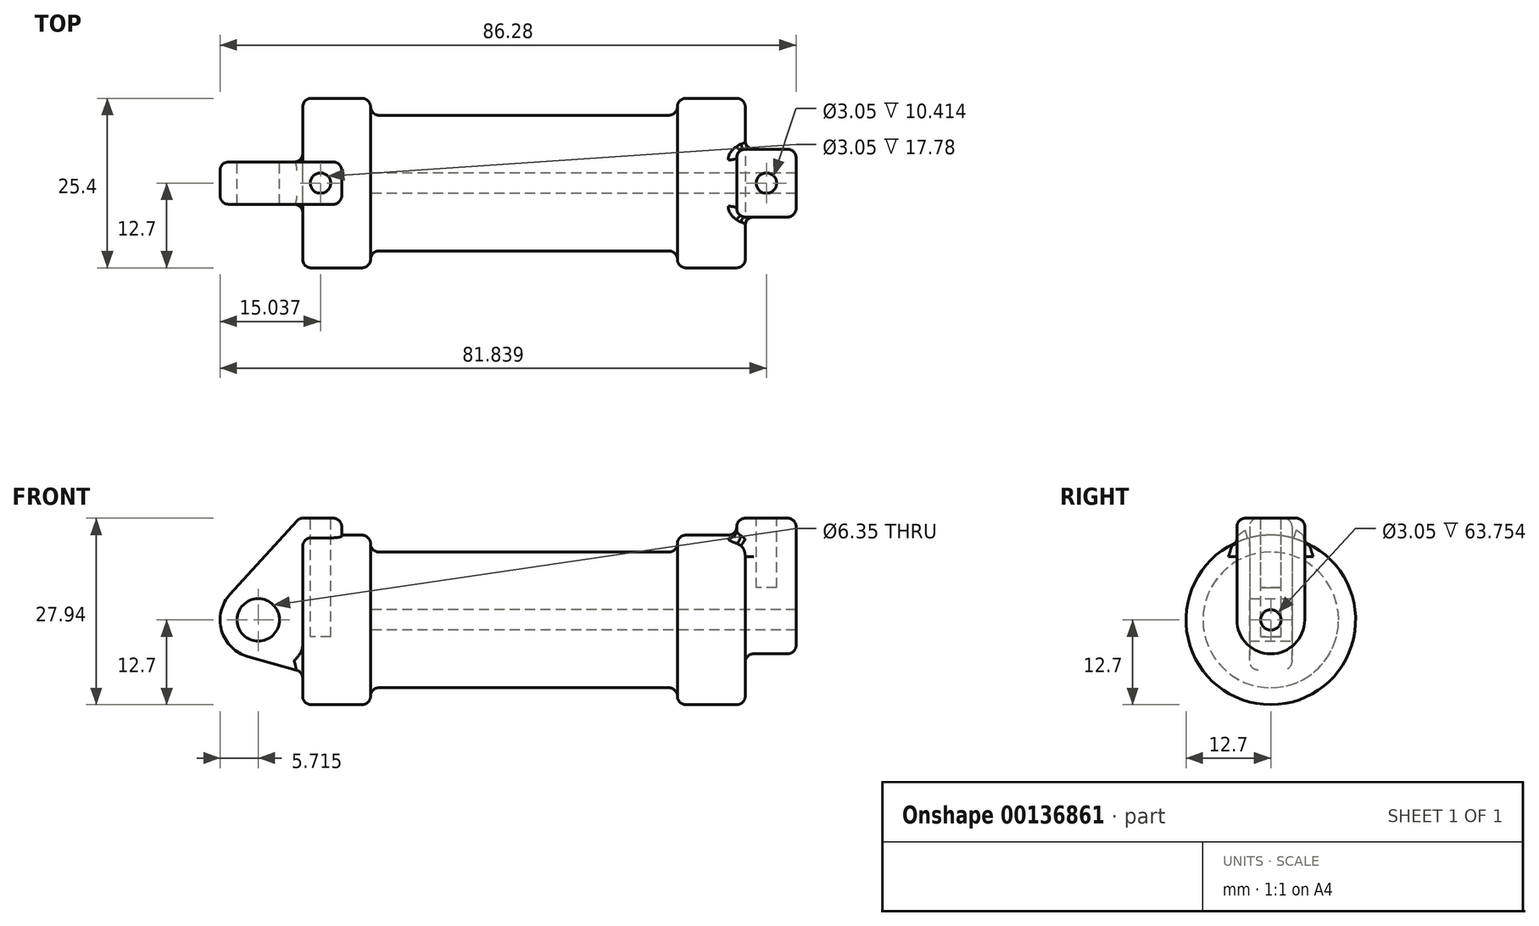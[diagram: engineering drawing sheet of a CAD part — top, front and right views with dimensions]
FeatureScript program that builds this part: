
annotation { "Feature Type Name" : "Feature", "Feature Type Description" : "" }
export const myFeature = defineFeature(function(context is Context, id is Id, definition is map)
    precondition{}
    {
        {
            var Q0;
            Q0=qCreatedBy(makeId("Front.planeOp"),FACE);
            var sketch = newSketch(context, id + "F0", { "sketchPlane" : qUnion([Q0])});
            skLineSegment(sketch, "E0", {"start": v(0, 0) * mm, "end": v(0, 12.7) * mm});
            skLineSegment(sketch, "E1", {"start": v(0, 12.7) * mm, "end": v(10.16, 12.7) * mm});
            skLineSegment(sketch, "E2", {"start": v(10.16, 12.7) * mm, "end": v(10.16, 10.16) * mm});
            skLineSegment(sketch, "E3", {"start": v(10.16, 10.16) * mm, "end": v(56.13, 10.16) * mm});
            skLineSegment(sketch, "E4", {"start": v(56.13, 10.16) * mm, "end": v(56.13, 12.7) * mm});
            skLineSegment(sketch, "E5", {"start": v(56.13, 12.7) * mm, "end": v(66.3, 12.7) * mm});
            skLineSegment(sketch, "E6", {"start": v(66.3, 12.7) * mm, "end": v(66.3, 0) * mm});
            skLineSegment(sketch, "E7", {"start": v(66.3, 0) * mm, "end": v(0, 0) * mm});
            skLineSegment(sketch, "E8", {"start": v(5.84, 15.24) * mm, "end": v(-0.5, 15.24) * mm});
            skLineSegment(sketch, "E9", {"start": v(-0.5, 15.24) * mm, "end": v(-10.88, 3.85) * mm});
            skLineSegment(sketch, "E10", {"start": v(0, 0) * mm, "end": v(-6.65, 0) * mm});
            skCircle(sketch, "E11", {"center": v(-6.65, 0) * mm, "radius": 5.72 * mm});
            skCircle(sketch, "E12", {"center": v(-6.65, 0) * mm, "radius": 3.18 * mm});
            skLineSegment(sketch, "E13", {"start": v(5.84, 15.24) * mm, "end": v(5.84, -9.4) * mm});
            skLineSegment(sketch, "E14", {"start": v(5.84, -9.4) * mm, "end": v(-8.18, -5.5) * mm});
            skSolve(sketch);
        }
        {
            var Q0;
            {var subQ0=sQuery(id+"F0.wireOp",EDGE,"E0");Q0=makeQuery(id+"F0.imprint","IMPRINT",FACE,{"disambiguationData":[TD([[makeQuery(id+"F0.imprint","IMPRINT",EDGE,{"derivedFrom":subQ0}),-1.0]])]});}
            var Q1;
            {var subQ0=sQuery(id+"F0.wireOp",EDGE,"E2");Q1=makeQuery(id+"F0.imprint","IMPRINT",FACE,{"disambiguationData":[TD([[makeQuery(id+"F0.imprint","IMPRINT",EDGE,{"derivedFrom":subQ0}),-1.0]])]});}
            var Q2;
            Q2=sQuery(id+"F0.wireOp",EDGE,"E7");
            revolve(context, id + "F1", {"entities" : qUnion([Q0, Q1]), "axis" : qUnion([Q2]), "revolveType" : RevolveType.FULL});
        }
        {
            var Q0;
            {var subQ3=sQuery(id+"F0.wireOp",EDGE,"E0");Q0=makeQuery(id+"F0.imprint","IMPRINT",FACE,{"disambiguationData":[TD([[makeQuery(id+"F0.imprint","IMPRINT",EDGE,{"derivedFrom":subQ3}),1.0]])]});}
            var Q1;
            {var subQ0=sQuery(id+"F0.wireOp",EDGE,"E0");Q1=makeQuery(id+"F0.imprint","IMPRINT",FACE,{"disambiguationData":[TD([[makeQuery(id+"F0.imprint","IMPRINT",EDGE,{"derivedFrom":subQ0}),-1.0]])]});}
            var Q2;
            {var subQ0=sQuery(id+"F0.wireOp",EDGE,"E14");Q2=makeQuery(id+"F0.imprint","IMPRINT",FACE,{"disambiguationData":[TD([[makeQuery(id+"F0.imprint","IMPRINT",EDGE,{"derivedFrom":subQ0}),-1.0]])]});}
            var Q3;
            {var subQ4=sQuery(id+"F0.wireOp",EDGE,"E12");Q3=makeQuery(id+"F0.imprint","IMPRINT",FACE,{"disambiguationData":[TD([[makeQuery(id+"F0.imprint","IMPRINT",EDGE,{"derivedFrom":subQ4}),-1.0]])]});}
            extrude(context, id + "F2", {"entities" : qUnion([Q0, Q1, Q2, Q3]), "operationType" : NewBodyOperationType.ADD, "endBound" : BoundingType.SYMMETRIC, "depth" : 6.35 * mm});
        }
        {
            var Q0;
            Q0=makeQuery(id+"F1.opRevolve","SWEPT_FACE",FACE,{"disambiguationData":[OSD([sQuery(id+"F0.wireOp",EDGE,"E6")])]});
            var sketch = newSketch(context, id + "F3", { "sketchPlane" : qUnion([Q0])});
            skCircle(sketch, "E15", {"center": v(0, 0) * mm, "radius": 1.52 * mm});
            skCircle(sketch, "E16", {"center": v(0, 0) * mm, "radius": 5.08 * mm});
            skLineSegment(sketch, "E17", {"start": v(5.08, 0) * mm, "end": v(5.08, 15.24) * mm});
            skLineSegment(sketch, "E18", {"start": v(-5.08, 15.24) * mm, "end": v(-5.08, 0) * mm});
            skLineSegment(sketch, "E19", {"start": v(-5.08, 15.24) * mm, "end": v(5.08, 15.24) * mm});
            skSolve(sketch);
        }
        {
            var Q0;
            Q0 = qSketchRegion(id + "F3", true);
            extrude(context, id + "F4", {"entities" : qUnion([Q0]), "operationType" : NewBodyOperationType.ADD, "depth" : 7.62 * mm, "hasSecondDirection" : true, "secondDirectionOppositeDirection" : true, "secondDirectionDepth" : 1.27 * mm});
        }
        {
            var Q0;
            Q0=makeQuery(id+"F4.boolean.opBoolean","SPLIT",FACE,{"disambiguationData":[TD([makeQuery(id+"F4.opExtrude","SWEPT_FACE",FACE,{"disambiguationData":[OSD([sQuery(id+"F3.wireOp",EDGE,"E15")])]})])],"derivedFrom":makeQuery(id+"F1.opRevolve","SWEPT_FACE",FACE,{"disambiguationData":[OSD([sQuery(id+"F0.wireOp",EDGE,"E6")])]})});
            var Q1;
            Q1=makeQuery(id+"F1.opRevolve","SWEPT_FACE",FACE,{"disambiguationData":[OSD([sQuery(id+"F0.wireOp",EDGE,"E2")])]});
            extrude(context, id + "F5", {"entities" : qUnion([Q0]), "operationType" : NewBodyOperationType.REMOVE, "endBound" : BoundingType.UP_TO_SURFACE, "oppositeDirection" : true, "endBoundEntityFace" : qUnion([Q1]), "depth" : 25.4 * mm});
        }
        {
            var Q0;
            Q0=makeQuery(id+"F4.opExtrude","SWEPT_FACE",FACE,{"disambiguationData":[OSD([sQuery(id+"F3.wireOp",EDGE,"E19")])]});
            var sketch = newSketch(context, id + "F6", { "sketchPlane" : qUnion([Q0])});
            skCircle(sketch, "E20", {"center": v(69.47, 0) * mm, "radius": 1.52 * mm});
            skPoint(sketch, "E20.centerSnap0", {"position": v(69.47, 5.08) * mm});
            skPoint(sketch, "E20.centerSnap1", {"position": v(65.02, 0) * mm});
            skSolve(sketch);
        }
        {
            var Q0;
            Q0 = qSketchRegion(id + "F6", true);
            extrude(context, id + "F7", {"entities" : qUnion([Q0]), "operationType" : NewBodyOperationType.REMOVE, "oppositeDirection" : true, "depth" : 10.4 * mm});
        }
        {
            var Q0;
            Q0=makeQuery(id+"F2.opExtrude","SWEPT_FACE",FACE,{"disambiguationData":[OSD([sQuery(id+"F0.wireOp",EDGE,"E8")])]});
            var sketch = newSketch(context, id + "F8", { "sketchPlane" : qUnion([Q0])});
            skCircle(sketch, "E21", {"center": v(2.67, 0) * mm, "radius": 1.52 * mm});
            skPoint(sketch, "E21.centerSnap0", {"position": v(2.67, 3.18) * mm});
            skPoint(sketch, "E21.centerSnap1", {"position": v(-0.5, 0) * mm});
            skSolve(sketch);
        }
        {
            var Q0;
            Q0 = qSketchRegion(id + "F8", true);
            extrude(context, id + "F9", {"entities" : qUnion([Q0]), "operationType" : NewBodyOperationType.REMOVE, "oppositeDirection" : true, "depth" : 17.78 * mm});
        }
        {
            var Q0;
            Q0=makeQuery(id+"F1.opRevolve","SWEPT_EDGE",EDGE,{"disambiguationData":[OSD([sQuery(id+"F0.wireOp",EDGE,"E2"),sQuery(id+"F0.wireOp",EDGE,"E3")])]});
            var Q1;
            Q1=makeQuery(id+"F1.opRevolve","SWEPT_EDGE",EDGE,{"disambiguationData":[OSD([sQuery(id+"F0.wireOp",EDGE,"E1"),sQuery(id+"F0.wireOp",EDGE,"E2")])]});
            var Q2;
            Q2=makeQuery(id+"F1.opRevolve","SWEPT_EDGE",EDGE,{"disambiguationData":[OSD([sQuery(id+"F0.wireOp",EDGE,"E0"),sQuery(id+"F0.wireOp",EDGE,"E1")])]});
            var Q3;
            Q3=makeQuery(id+"F1.opRevolve","SWEPT_EDGE",EDGE,{"disambiguationData":[OSD([sQuery(id+"F0.wireOp",EDGE,"E4"),sQuery(id+"F0.wireOp",EDGE,"E5")])]});
            var Q4;
            Q4=makeQuery(id+"F1.opRevolve","SWEPT_EDGE",EDGE,{"disambiguationData":[OSD([sQuery(id+"F0.wireOp",EDGE,"E5"),sQuery(id+"F0.wireOp",EDGE,"E6")])]});
            var Q5;
            Q5=makeQuery(id+"F1.opRevolve","SWEPT_EDGE",EDGE,{"disambiguationData":[OSD([sQuery(id+"F0.wireOp",EDGE,"E3"),sQuery(id+"F0.wireOp",EDGE,"E4")])]});
            fillet(context, id + "F10", {"entities" : qUnion([Q0, Q1, Q2, Q3, Q4, Q5]), "radius" : 1.27 * mm, "tangentPropagation" : true, "allowEdgeOverflow" : false});
        }
        {
            var Q0;
            Q0=makeQuery(id+"F2.opExtrude","CAP_EDGE",EDGE,{"disambiguationData":[OSD([sQuery(id+"F0.wireOp",EDGE,"E9")])],"isStart":false});
            var Q1;
            Q1=makeQuery(id+"F2.opExtrude","CAP_EDGE",EDGE,{"disambiguationData":[OSD([sQuery(id+"F0.wireOp",EDGE,"E11")])],"isStart":true});
            var Q2;
            Q2=makeQuery(id+"F2.boolean.opBoolean","INTERSECT",EDGE,{"derivedFrom":[makeQuery(id+"F1.opRevolve","SWEPT_FACE",FACE,{"disambiguationData":[OSD([sQuery(id+"F0.wireOp",EDGE,"E0")])]}),makeQuery(id+"F2.opExtrude","SWEPT_FACE",FACE,{"disambiguationData":[OSD([sQuery(id+"F0.wireOp",EDGE,"E14")])]})]});
            var Q3;
            Q3=makeQuery(id+"F2.opExtrude","CAP_EDGE",EDGE,{"disambiguationData":[OSD([sQuery(id+"F0.wireOp",EDGE,"E8")])],"isStart":false});
            var Q4;
            Q4=makeQuery(id+"F2.opExtrude","SWEPT_EDGE",EDGE,{"disambiguationData":[OSD([sQuery(id+"F0.wireOp",EDGE,"E8"),sQuery(id+"F0.wireOp",EDGE,"E13")])]});
            var Q5;
            Q5=makeQuery(id+"F2.opExtrude","CAP_EDGE",EDGE,{"disambiguationData":[OSD([sQuery(id+"F0.wireOp",EDGE,"E8")])],"isStart":true});
            var Q6;
            Q6=makeQuery(id+"F2.opExtrude","SWEPT_EDGE",EDGE,{"disambiguationData":[OSD([sQuery(id+"F0.wireOp",EDGE,"E8"),sQuery(id+"F0.wireOp",EDGE,"E9")])]});
            var Q7;
            Q7=makeQuery(id+"F2.opExtrude","CAP_EDGE",EDGE,{"disambiguationData":[OSD([sQuery(id+"F0.wireOp",EDGE,"E13")])],"isStart":false});
            var Q8;
            Q8=makeQuery(id+"F2.opExtrude","CAP_EDGE",EDGE,{"disambiguationData":[OSD([sQuery(id+"F0.wireOp",EDGE,"E13")])],"isStart":true});
            fillet(context, id + "F11", {"entities" : qUnion([Q0, Q1, Q2, Q3, Q4, Q5, Q6, Q7, Q8]), "radius" : 1.27 * mm, "tangentPropagation" : true, "allowEdgeOverflow" : false});
        }
        {
            var Q0;
            Q0=makeQuery(id+"F4.opExtrude","CAP_EDGE",EDGE,{"disambiguationData":[OSD([sQuery(id+"F3.wireOp",EDGE,"E18")])],"isStart":false});
            var Q1;
            Q1=makeQuery(id+"F4.boolean.opBoolean","INTERSECT",EDGE,{"derivedFrom":[makeQuery(id+"F1.opRevolve","SWEPT_FACE",FACE,{"disambiguationData":[OSD([sQuery(id+"F0.wireOp",EDGE,"E6")])]}),makeQuery(id+"F4.opExtrude","SWEPT_FACE",FACE,{"disambiguationData":[OSD([sQuery(id+"F3.wireOp",EDGE,"E18")])]})]});
            var Q2;
            Q2=makeQuery(id+"F4.opExtrude","SWEPT_EDGE",EDGE,{"disambiguationData":[OSD([sQuery(id+"F3.wireOp",EDGE,"E18"),sQuery(id+"F3.wireOp",EDGE,"E19")])]});
            var Q3;
            Q3=makeQuery(id+"F4.opExtrude","CAP_EDGE",EDGE,{"disambiguationData":[OSD([sQuery(id+"F3.wireOp",EDGE,"E19")])],"isStart":false});
            var Q4;
            Q4=makeQuery(id+"F4.opExtrude","SWEPT_EDGE",EDGE,{"disambiguationData":[OSD([sQuery(id+"F3.wireOp",EDGE,"E17"),sQuery(id+"F3.wireOp",EDGE,"E19")])]});
            var Q5;
            Q5=makeQuery(id+"F4.opExtrude","CAP_EDGE",EDGE,{"disambiguationData":[OSD([sQuery(id+"F3.wireOp",EDGE,"E19")])],"isStart":true});
            var Q6;
            Q6=makeQuery(id+"F4.boolean.opBoolean","INTERSECT",EDGE,{"derivedFrom":[makeQuery(id+"F1.opRevolve","SWEPT_FACE",FACE,{"disambiguationData":[OSD([sQuery(id+"F0.wireOp",EDGE,"E5")])]}),makeQuery(id+"F4.opExtrude","CAP_FACE",FACE,{"disambiguationData":[OSD([sQuery(id+"F3.wireOp",EDGE,"E15"),sQuery(id+"F3.wireOp",EDGE,"E16"),sQuery(id+"F3.wireOp",EDGE,"E17"),sQuery(id+"F3.wireOp",EDGE,"E18"),sQuery(id+"F3.wireOp",EDGE,"E19")])],"isStart":true})]});
            var Q7;
            Q7=makeQuery(id+"F4.opExtrude","CAP_EDGE",EDGE,{"disambiguationData":[OSD([sQuery(id+"F3.wireOp",EDGE,"E18")])],"isStart":true});
            var Q8;
            Q8=makeQuery(id+"F4.opExtrude","CAP_EDGE",EDGE,{"disambiguationData":[OSD([sQuery(id+"F3.wireOp",EDGE,"E17")])],"isStart":true});
            fillet(context, id + "F12", {"entities" : qUnion([Q0, Q1, Q2, Q3, Q4, Q5, Q6, Q7, Q8]), "radius" : 1.27 * mm, "tangentPropagation" : true, "allowEdgeOverflow" : false});
        }
    });
